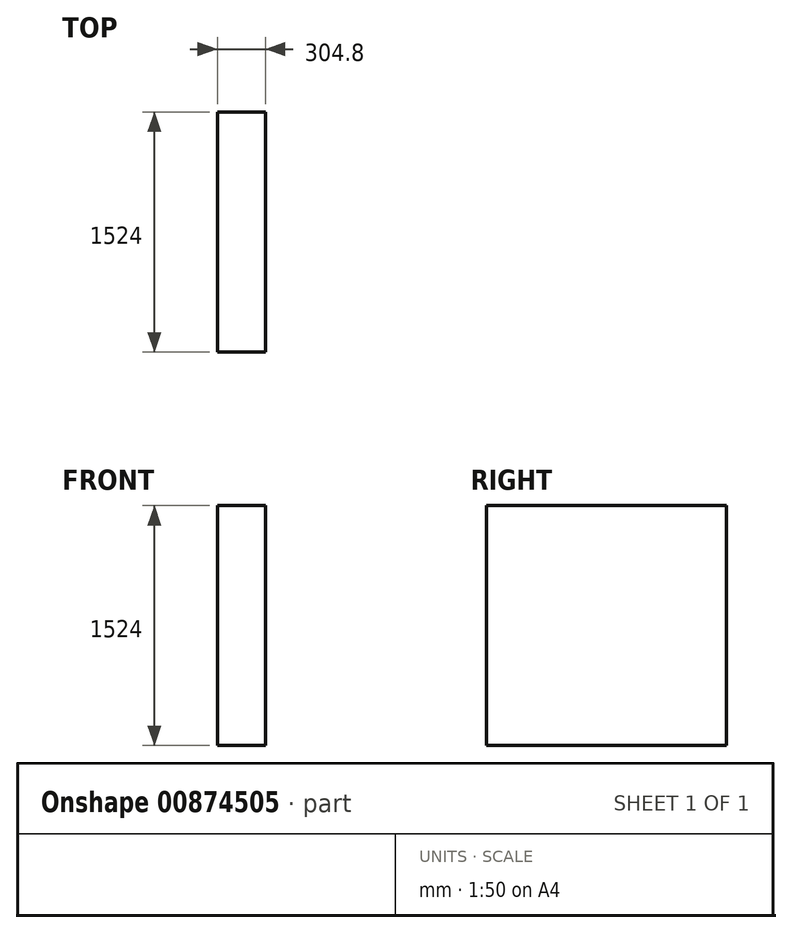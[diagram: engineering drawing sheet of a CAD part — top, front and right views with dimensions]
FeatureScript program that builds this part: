
annotation { "Feature Type Name" : "Feature", "Feature Type Description" : "" }
export const myFeature = defineFeature(function(context is Context, id is Id, definition is map)
    precondition{}
    {
        {
            var Q0;
            Q0=qCreatedBy(makeId("Right.planeOp"),FACE);
            var sketch = newSketch(context, id + "F0", { "sketchPlane" : qUnion([Q0])});
            skLineSegment(sketch, "E0.bottom", {"start": v(0, 0) * mm, "end": v(-1524, 0) * mm});
            skLineSegment(sketch, "E0.top", {"start": v(0, 1524) * mm, "end": v(-1524, 1524) * mm});
            skLineSegment(sketch, "E0.left", {"start": v(0, 0) * mm, "end": v(0, 1524) * mm});
            skLineSegment(sketch, "E0.right", {"start": v(-1524, 0) * mm, "end": v(-1524, 1524) * mm});
            skSolve(sketch);
        }
        {
            var Q0;
            Q0=makeQuery(id+"F0.imprint","IMPRINT",FACE,{"disambiguationData":[TD([[makeQuery(id+"F0.imprint","IMPRINT",EDGE,{"derivedFrom":sQuery(id+"F0.wireOp",EDGE,"E0.bottom")}),-1.0]])]});
            extrude(context, id + "F1", {"entities" : qUnion([Q0]), "depth" : 304.8 * mm, "offsetDistance" : 25.4 * mm});
        }
    });
